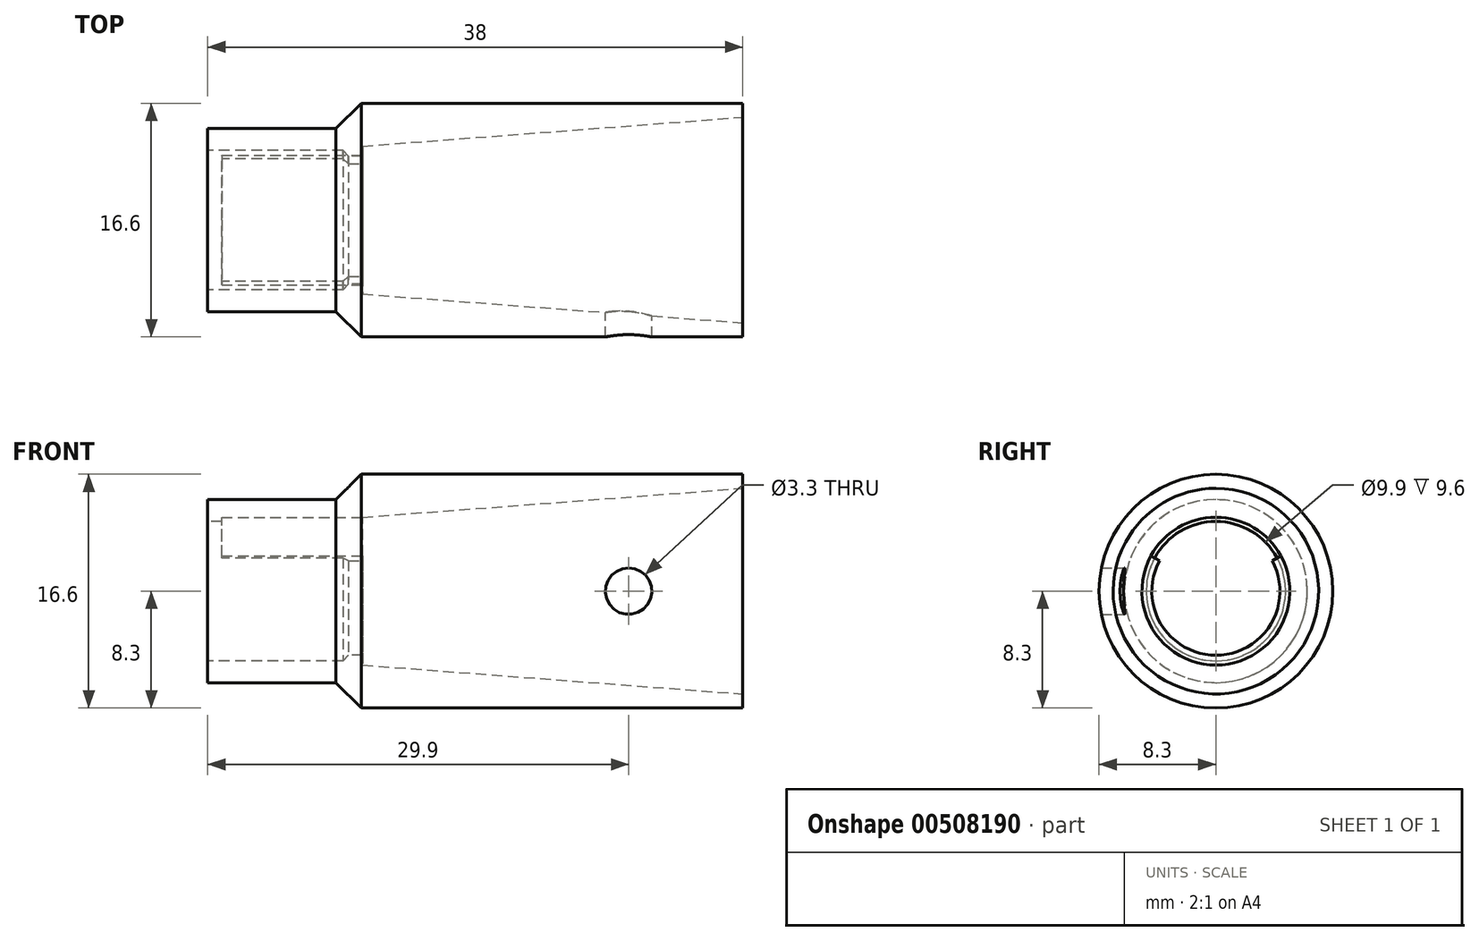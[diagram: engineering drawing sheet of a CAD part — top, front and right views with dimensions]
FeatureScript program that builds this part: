
annotation { "Feature Type Name" : "Feature", "Feature Type Description" : "" }
export const myFeature = defineFeature(function(context is Context, id is Id, definition is map)
    precondition{}
    {
        {
            var Q0;
            Q0=qCreatedBy(makeId("Front.planeOp"),FACE);
            var sketch = newSketch(context, id + "F0", { "sketchPlane" : qUnion([Q0])});
            skLineSegment(sketch, "E0", {"start": v(0, 0) * mm, "end": v(38, 0) * mm, "construction": true});
            skLineSegment(sketch, "E1", {"start": v(0, 4.95) * mm, "end": v(9.6, 4.95) * mm});
            skLineSegment(sketch, "E2", {"start": v(9, 6.5) * mm, "end": v(9, 8.3) * mm});
            skLineSegment(sketch, "E3", {"start": v(9, 8.3) * mm, "end": v(38, 8.3) * mm});
            skLineSegment(sketch, "E4", {"start": v(38, 8.3) * mm, "end": v(38, 7.3) * mm});
            skLineSegment(sketch, "E5", {"start": v(9.6, 4.95) * mm, "end": v(10, 4.55) * mm});
            skLineSegment(sketch, "E6", {"start": v(10, 4.55) * mm, "end": v(11, 4.55) * mm});
            skLineSegment(sketch, "E7", {"start": v(11, 4.55) * mm, "end": v(11, 5.25) * mm});
            skLineSegment(sketch, "E8", {"start": v(11, 5.25) * mm, "end": v(38, 7.3) * mm});
            skLineSegment(sketch, "E9", {"start": v(9, 6.5) * mm, "end": v(0, 6.5) * mm});
            skLineSegment(sketch, "E10", {"start": v(0, 4.95) * mm, "end": v(0, 6.5) * mm});
            skSolve(sketch);
        }
        {
            var Q0;
            Q0 = qSketchRegion(id + "F0", true);
            var Q1;
            Q1=sQuery(id+"F0.wireOp",EDGE,"E0");
            revolve(context, id + "F1", {"surfaceOperationType" : NewSurfaceOperationType.NEW, "entities" : qUnion([Q0]), "axis" : qUnion([Q1]), "revolveType" : RevolveType.FULL});
        }
        {
            var Q0;
            Q0=makeQuery(id+"F1.opRevolve","SWEPT_EDGE",EDGE,{"disambiguationData":[OSD([sQuery(id+"F0.wireOp",EDGE,"E2"),sQuery(id+"F0.wireOp",EDGE,"E3")])]});
            chamfer(context, id + "F2", {"entities" : qUnion([Q0]), "width" : 1.9 * mm, "tangentPropagation" : true});
        }
        {
            var Q0;
            Q0=makeQuery(id+"F1.opRevolve","SWEPT_FACE",FACE,{"disambiguationData":[OSD([sQuery(id+"F0.wireOp",EDGE,"E7")])]});
            var sketch = newSketch(context, id + "F3", { "sketchPlane" : qUnion([Q0])});
            skArc(sketch, "E11.0", {"start": v(-4, 2.17) * mm, "mid": v(0, 4.55) * mm, "end": v(4, 2.17) * mm});
            skArc(sketch, "E12", {"start": v(4.62, 2.5) * mm, "mid": v(0, 5.25) * mm, "end": v(-4.62, 2.5) * mm});
            skLineSegment(sketch, "E13", {"start": v(-4, 2.17) * mm, "end": v(-4.62, 2.5) * mm});
            skLineSegment(sketch, "E14", {"start": v(4.62, 2.5) * mm, "end": v(4, 2.17) * mm});
            skSolve(sketch);
        }
        {
            var Q0;
            Q0 = qSketchRegion(id + "F3", true);
            extrude(context, id + "F4", {"entities" : qUnion([Q0]), "operationType" : NewBodyOperationType.REMOVE, "oppositeDirection" : true, "depth" : 10 * mm, "offsetDistance" : 25 * mm});
        }
        {
            var Q0;
            Q0=qCreatedBy(makeId("Front.planeOp"), FACE);
            var sketch = newSketch(context, id + "F5", { "sketchPlane" : qUnion([Q0])});
            skCircle(sketch, "E15", {"center": v(29.9, 0) * mm, "radius": 1.65 * mm});
            skSolve(sketch);
        }
        {
            var Q0;
            Q0 = qSketchRegion(id + "F5", true);
            extrude(context, id + "F6", {"entities" : qUnion([Q0]), "operationType" : NewBodyOperationType.REMOVE, "endBound" : BoundingType.THROUGH_ALL, "depth" : 25 * mm, "offsetDistance" : 25 * mm});
        }
    });
